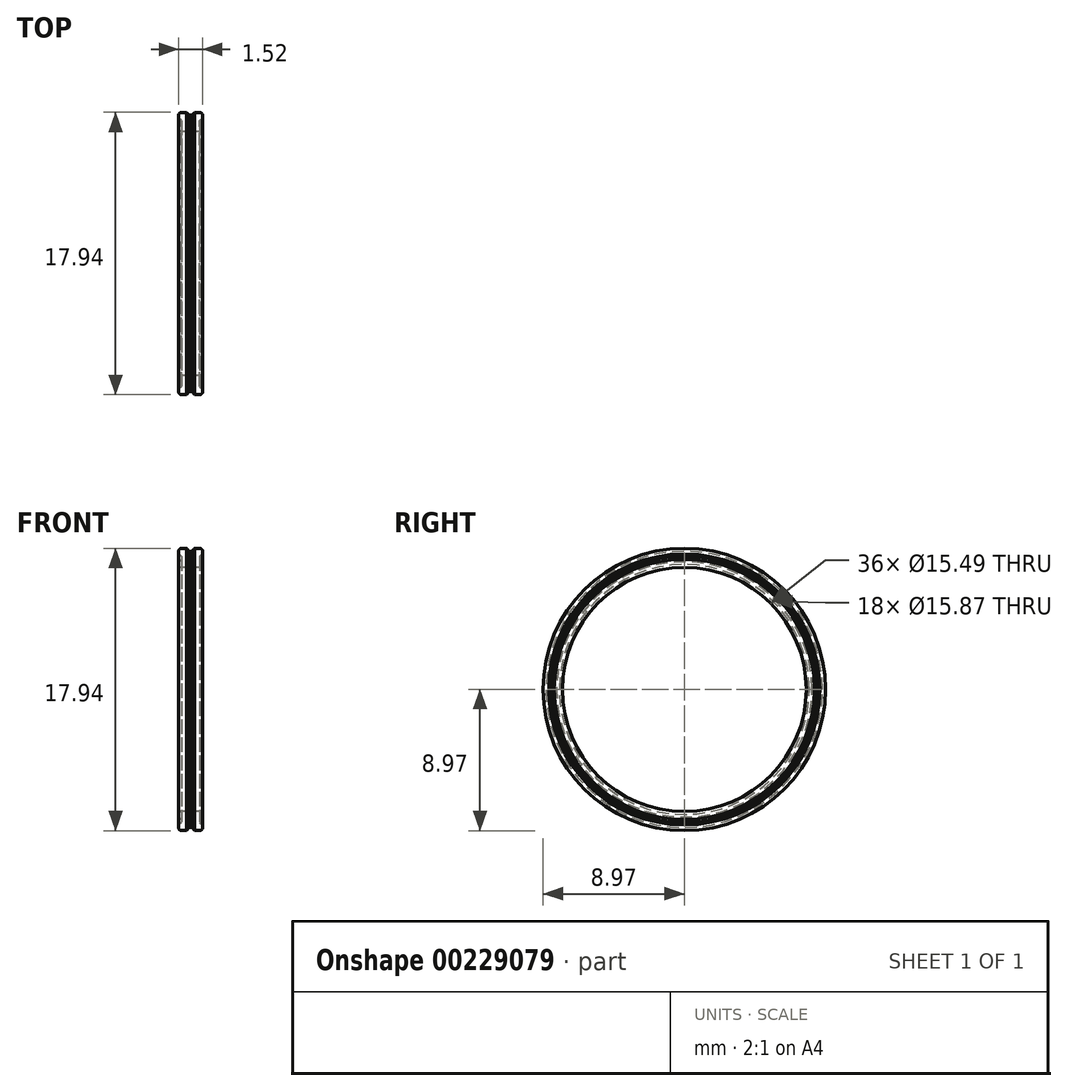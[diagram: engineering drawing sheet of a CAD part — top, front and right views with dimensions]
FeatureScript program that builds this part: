
annotation { "Feature Type Name" : "Feature", "Feature Type Description" : "" }
export const myFeature = defineFeature(function(context is Context, id is Id, definition is map)
    precondition{}
    {
        {
            var Q0;
            Q0=qCreatedBy(makeId("Front.planeOp"),FACE);
            var sketch = newSketch(context, id + "F0", { "sketchPlane" : qUnion([Q0])});
            skLineSegment(sketch, "E0", {"start": v(0, 7.75) * mm, "end": v(0.5, 7.75) * mm});
            skLineSegment(sketch, "E1", {"start": v(1.52, 7.75) * mm, "end": v(1.52, 8.11) * mm});
            skLineSegment(sketch, "E2", {"start": v(1.52, 8.97) * mm, "end": v(1, 8.97) * mm});
            skLineSegment(sketch, "E3", {"start": v(0, 8.97) * mm, "end": v(0, 8.6) * mm});
            skLineSegment(sketch, "E4", {"start": v(0.5, 7.75) * mm, "end": v(0.67, 7.94) * mm});
            skLineSegment(sketch, "E5", {"start": v(1.52, 7.75) * mm, "end": v(1, 7.75) * mm});
            skLineSegment(sketch, "E6", {"start": v(1, 7.75) * mm, "end": v(0.85, 7.94) * mm});
            skLineSegment(sketch, "E7", {"start": v(0.76, 7.94) * mm, "end": v(0.85, 7.94) * mm});
            skLineSegment(sketch, "E8", {"start": v(0.76, 7.94) * mm, "end": v(0.67, 7.94) * mm});
            skLineSegment(sketch, "E9.MirrorCS", {"start": v(0.5, 8.97) * mm, "end": v(0.67, 8.78) * mm});
            skLineSegment(sketch, "E10.MirrorCS", {"start": v(0.76, 8.78) * mm, "end": v(0.67, 8.78) * mm});
            skLineSegment(sketch, "E11.MirrorCS", {"start": v(0.76, 8.78) * mm, "end": v(0.85, 8.78) * mm});
            skLineSegment(sketch, "E12.MirrorCS", {"start": v(1, 8.97) * mm, "end": v(0.85, 8.78) * mm});
            skLineSegment(sketch, "E13", {"start": v(0, 8.36) * mm, "end": v(0.2, 8.36) * mm});
            skLineSegment(sketch, "E14", {"start": v(0.2, 8.36) * mm, "end": v(0.2, 8.45) * mm});
            skLineSegment(sketch, "E15", {"start": v(0.2, 8.36) * mm, "end": v(0.2, 8.27) * mm});
            skLineSegment(sketch, "E16", {"start": v(0, 8.6) * mm, "end": v(0.2, 8.45) * mm});
            skLineSegment(sketch, "E17", {"start": v(0, 8.11) * mm, "end": v(0.2, 8.27) * mm});
            skLineSegment(sketch, "E18.MirrorCS", {"start": v(1.52, 8.6) * mm, "end": v(1.33, 8.45) * mm});
            skLineSegment(sketch, "E19.MirrorCS", {"start": v(1.33, 8.36) * mm, "end": v(1.33, 8.45) * mm});
            skLineSegment(sketch, "E20.MirrorCS", {"start": v(1.33, 8.36) * mm, "end": v(1.33, 8.27) * mm});
            skLineSegment(sketch, "E21.MirrorCS", {"start": v(1.52, 8.11) * mm, "end": v(1.33, 8.27) * mm});
            skLineSegment(sketch, "E22.trimOffspring", {"start": v(0, 8.11) * mm, "end": v(0, 7.75) * mm});
            skLineSegment(sketch, "E23.trimOffspring", {"start": v(1.52, 8.6) * mm, "end": v(1.52, 8.97) * mm});
            skLineSegment(sketch, "E24.trimOffspring", {"start": v(0.5, 8.97) * mm, "end": v(0, 8.97) * mm});
            skLineSegment(sketch, "E25.trimOffspring", {"start": v(1, 7.75) * mm, "end": v(1.52, 7.75) * mm});
            skLineSegment(sketch, "E26", {"start": v(0, 0) * mm, "end": v(0.95, 0) * mm});
            skSolve(sketch);
        }
        {
            var Q0;
            Q0 = qSketchRegion(id + "F0", true);
            var Q1;
            Q1=sQuery(id+"F0.wireOp",EDGE,"E26");
            revolve(context, id + "F1", {"entities" : qUnion([Q0]), "axis" : qUnion([Q1]), "revolveType" : RevolveType.FULL});
        }
        {
            var Q0;
            Q0=makeQuery(id+"F1.opRevolve","SWEPT_EDGE",EDGE,{"disambiguationData":[OSD([sQuery(id+"F0.wireOp",EDGE,"E3"),sQuery(id+"F0.wireOp",EDGE,"E24.trimOffspring")])]});
            var Q1;
            Q1=makeQuery(id+"F1.opRevolve","SWEPT_EDGE",EDGE,{"disambiguationData":[OSD([sQuery(id+"F0.wireOp",EDGE,"E2"),sQuery(id+"F0.wireOp",EDGE,"E23.trimOffspring")])]});
            var Q2;
            Q2=makeQuery(id+"F1.opRevolve","SWEPT_EDGE",EDGE,{"disambiguationData":[OSD([sQuery(id+"F0.wireOp",EDGE,"E0"),sQuery(id+"F0.wireOp",EDGE,"E22.trimOffspring")])]});
            var Q3;
            Q3=makeQuery(id+"F1.opRevolve","SWEPT_EDGE",EDGE,{"disambiguationData":[OSD([sQuery(id+"F0.wireOp",EDGE,"E1"),sQuery(id+"F0.wireOp",EDGE,"E25.trimOffspring")])]});
            fillet(context, id + "F2", {"entities" : qUnion([Q0, Q1, Q2, Q3]), "radius" : 0.2 * mm, "tangentPropagation" : true, "allowEdgeOverflow" : false});
        }
    });
